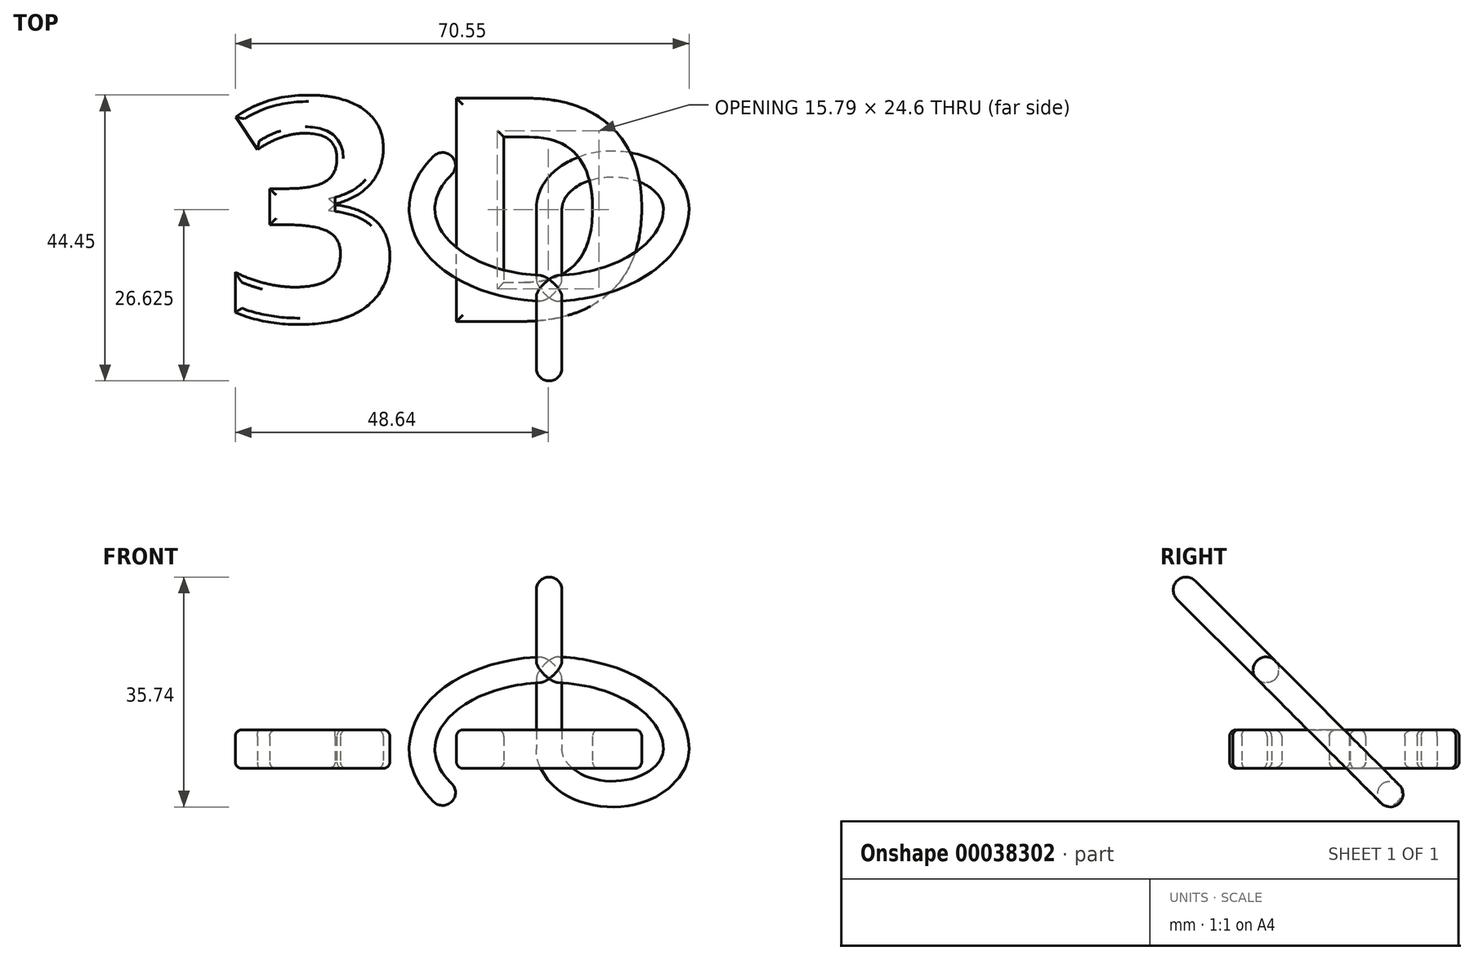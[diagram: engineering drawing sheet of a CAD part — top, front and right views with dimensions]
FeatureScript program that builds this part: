
annotation { "Feature Type Name" : "Feature", "Feature Type Description" : "" }
export const myFeature = defineFeature(function(context is Context, id is Id, definition is map)
    precondition{}
    {
        {
            var Q0;
            Q0=qCreatedBy(makeId("Top.planeOp"),FACE);
            var sketch = newSketch(context, id + "F0", { "sketchPlane" : qUnion([Q0])});
            skText(sketch, "E0", { "text": "3", "fontName": "OpenSans-Bold.ttf"});
            skPoint(sketch, "E1", {"position": v(-17.94, 0) * mm});
            skText(sketch, "E2", { "text": "D", "fontName": "OpenSans-Bold.ttf"});
            skPoint(sketch, "E3", {"position": v(17.58, 0) * mm});
            const initialGuessF0  = {"E0": [-0.03087, -0.0175, 1, 0, 0.035], "E2": [0.001, -0.0175, 1, 0, 0.035]};
            skSetInitialGuess(sketch, initialGuessF0);
            skSolve(sketch);
        }
        {
            var Q0;
            Q0 = qSketchRegion(id + "F0", true);
            extrude(context, id + "F1", {"entities" : qUnion([Q0]), "endBound" : BoundingType.SYMMETRIC, "depth" : 6 * mm});
        }
        {
            var Q0;
            Q0=qCreatedBy(makeId("Front.planeOp"),FACE);
            var sketch = newSketch(context, id + "F2", { "sketchPlane" : qUnion([Q0])});
            skEllipticalArc(sketch, "E4", {});
            skArc(sketch, "E5", {"start": v(19.76, 0) * mm, "mid": v(29.65, -9.88) * mm, "end": v(39.53, 0) * mm});
            skLineSegment(sketch, "E6", {"start": v(19.76, 0) * mm, "end": v(19.76, 35) * mm});
            skPoint(sketch, "E6.endSnap0", {"position": v(19.76, 17.5) * mm});
            skLineSegment(sketch, "E7", {"start": v(19.76, 0) * mm, "end": v(3.2, -9.56) * mm, "construction": true});
            skLineSegment(sketch, "E8", {"start": v(5.37, 0) * mm, "end": v(34.16, 0) * mm, "construction": true});
            const initialGuessF2  = {"E4": [0.0197646484375, 0, 1, 0, 0.0197646484375, 0.0175, 0, 3.71941767693255]};
            skSetInitialGuess(sketch, initialGuessF2);
            skSolve(sketch);
        }
        {
            var Q0;
            Q0=sQuery(id+"F2.wireOp",VERTEX,"E6.end");
            var Q1;
            Q1=qCreatedBy(makeId("Top.planeOp"),FACE);
            cPlane(context, id + "F3", {"entities" : qUnion([Q0, Q1]), "cplaneType" : CPlaneType.PLANE_POINT, "offset" : 150 * mm, "width" : 150 * mm, "height" : 150 * mm});
        }
        {
            var Q0;
            Q0=qCreatedBy(id+"F3.planeOp",FACE);
            var sketch = newSketch(context, id + "F4", { "sketchPlane" : qUnion([Q0])});
            skCircle(sketch, "E9", {"center": v(19.76, 0) * mm, "radius": 2 * mm});
            skSolve(sketch);
        }
        {
            var Q0;
            Q0=makeQuery(id+"F4.imprint","IMPRINT",FACE,{"disambiguationData":[TD([[makeQuery(id+"F4.imprint","IMPRINT",EDGE,{"derivedFrom":sQuery(id+"F4.wireOp",EDGE,"E9")}),1.0]])]});
            var Q1;
            Q1=sQuery(id+"F2.wireOp",EDGE,"E6");
            var Q2;
            Q2=sQuery(id+"F2.wireOp",EDGE,"E5");
            sweep(context, id + "F5", {"profiles" : qUnion([Q0]), "path" : qUnion([Q1, Q2])});
        }
        {
            var Q0;
            Q0=makeQuery(id+"F5.opSweep","CAP_FACE",FACE,{"disambiguationData":[OSD([sQuery(id+"F2.wireOp",VERTEX,"E5.end"),sQuery(id+"F4.wireOp",EDGE,"E9")])],"isStart":false});
            var Q1;
            Q1=sQuery(id+"F2.wireOp",EDGE,"E4");
            sweep(context, id + "F6", {"operationType" : NewBodyOperationType.ADD, "profiles" : qUnion([Q0]), "path" : qUnion([Q1])});
        }
        {
            var Q0;
            Q0=makeQuery(id+"F5.opSweep","CAP_FACE",FACE,{"disambiguationData":[OSD([sQuery(id+"F2.wireOp",VERTEX,"E6.end"),sQuery(id+"F4.wireOp",EDGE,"E9")])],"isStart":true});
            var sketch = newSketch(context, id + "F7", { "sketchPlane" : qUnion([Q0])});
            skLineSegment(sketch, "E10", {"start": v(17.76, 0) * mm, "end": v(21.76, 0) * mm});
            skSolve(sketch);
        }
        {
            var Q0;
            {var subQ1=sQuery(id+"F7.wireOp",EDGE,"E10");Q0=makeQuery(id+"F7.imprint","IMPRINT",FACE,{"disambiguationData":[TD([[makeQuery(id+"F7.imprint","IMPRINT",EDGE,{"derivedFrom":subQ1}),-1.0]])]});}
            var Q1;
            Q1=sQuery(id+"F7.wireOp",EDGE,"E10");
            revolve(context, id + "F8", {"operationType" : NewBodyOperationType.ADD, "entities" : qUnion([Q0]), "axis" : qUnion([Q1]), "revolveType" : RevolveType.FULL});
        }
        {
            var Q0;
            Q0=makeQuery(id+"F6.opSweep","CAP_FACE",FACE,{"disambiguationData":[OSD([sQuery(id+"F2.wireOp",VERTEX,"E4.end"),sQuery(id+"F2.wireOp",VERTEX,"E5.end"),sQuery(id+"F4.wireOp",EDGE,"E9")])],"isStart":false});
            var sketch = newSketch(context, id + "F9", { "sketchPlane" : qUnion([Q0])});
            skLineSegment(sketch, "E11", {"start": v(-3.08, 2) * mm, "end": v(-3.08, -2) * mm});
            skSolve(sketch);
        }
        {
            var Q0;
            {var subQ1=sQuery(id+"F9.wireOp",EDGE,"E11");Q0=makeQuery(id+"F9.imprint","IMPRINT",FACE,{"disambiguationData":[TD([[makeQuery(id+"F9.imprint","IMPRINT",EDGE,{"derivedFrom":subQ1}),-1.0]])]});}
            var Q1;
            Q1=sQuery(id+"F9.wireOp",EDGE,"E11");
            revolve(context, id + "F10", {"operationType" : NewBodyOperationType.ADD, "entities" : qUnion([Q0]), "axis" : qUnion([Q1]), "revolveType" : RevolveType.FULL});
        }
        {
            var Q0;
            Q0=makeQuery(id+"F5.opSweep","SWEPT_BODY",BODY,{"disambiguationData":[OSD([sQuery(id+"F2.wireOp",EDGE,"E5"),sQuery(id+"F4.wireOp",EDGE,"E9")])]});
            var Q1;
            Q1=sQuery(id+"F2.wireOp",EDGE,"E8");
            transform(context, id + "F11", {"entities" : qUnion([Q0]), "transformType" : TransformType.ROTATION, "transformAxis" : qUnion([Q1]), "angle" : 45 * degree, "makeCopy" : false});
        }
        {
            var Q0;
            Q0=makeQuery(id+"F1.opExtrude","CAP_EDGE",EDGE,{"disambiguationData":[OSD([sQuery(id+"F0.wireOp",EDGE,"E0.sketch_text.stroke-6")])],"isStart":false});
            var Q1;
            Q1=makeQuery(id+"F1.opExtrude","CAP_EDGE",EDGE,{"disambiguationData":[OSD([sQuery(id+"F0.wireOp",EDGE,"E0.sketch_text.stroke-0")])],"isStart":false});
            var Q2;
            Q2=makeQuery(id+"F1.opExtrude","CAP_EDGE",EDGE,{"disambiguationData":[OSD([sQuery(id+"F0.wireOp",EDGE,"E0.sketch_text.stroke-23")])],"isStart":false});
            var Q3;
            Q3=makeQuery(id+"F1.opExtrude","CAP_EDGE",EDGE,{"disambiguationData":[OSD([sQuery(id+"F0.wireOp",EDGE,"E0.sketch_text.stroke-21")])],"isStart":false});
            var Q4;
            Q4=makeQuery(id+"F1.opExtrude","CAP_EDGE",EDGE,{"disambiguationData":[OSD([sQuery(id+"F0.wireOp",EDGE,"E0.sketch_text.stroke-16")])],"isStart":false});
            var Q5;
            Q5=makeQuery(id+"F1.opExtrude","CAP_EDGE",EDGE,{"disambiguationData":[OSD([sQuery(id+"F0.wireOp",EDGE,"E0.sketch_text.stroke-14")])],"isStart":false});
            var Q6;
            Q6=makeQuery(id+"F1.opExtrude","CAP_EDGE",EDGE,{"disambiguationData":[OSD([sQuery(id+"F0.wireOp",EDGE,"E0.sketch_text.stroke-8")])],"isStart":false});
            var Q7;
            Q7=makeQuery(id+"F1.opExtrude","CAP_EDGE",EDGE,{"disambiguationData":[OSD([sQuery(id+"F0.wireOp",EDGE,"E0.sketch_text.stroke-30")])],"isStart":false});
            var Q8;
            Q8=makeQuery(id+"F1.opExtrude","CAP_EDGE",EDGE,{"disambiguationData":[OSD([sQuery(id+"F0.wireOp",EDGE,"E0.sketch_text.stroke-31")])],"isStart":false});
            var Q9;
            Q9=makeQuery(id+"F1.opExtrude","CAP_EDGE",EDGE,{"disambiguationData":[OSD([sQuery(id+"F0.wireOp",EDGE,"E0.sketch_text.stroke-36")])],"isStart":false});
            var Q10;
            Q10=makeQuery(id+"F1.opExtrude","CAP_EDGE",EDGE,{"disambiguationData":[OSD([sQuery(id+"F0.wireOp",EDGE,"E0.sketch_text.stroke-35")])],"isStart":false});
            var Q11;
            Q11=makeQuery(id+"F1.opExtrude","CAP_FACE",FACE,{"disambiguationData":[OSD([sQuery(id+"F0.wireOp",EDGE,"E0.sketch_text.stroke-27"),sQuery(id+"F0.wireOp",EDGE,"E0.sketch_text.stroke-28"),sQuery(id+"F0.wireOp",EDGE,"E0.sketch_text.stroke-29"),sQuery(id+"F0.wireOp",EDGE,"E0.sketch_text.stroke-30"),sQuery(id+"F0.wireOp",EDGE,"E0.sketch_text.stroke-31"),sQuery(id+"F0.wireOp",EDGE,"E0.sketch_text.stroke-32"),sQuery(id+"F0.wireOp",EDGE,"E0.sketch_text.stroke-33"),sQuery(id+"F0.wireOp",EDGE,"E0.sketch_text.stroke-34"),sQuery(id+"F0.wireOp",EDGE,"E0.sketch_text.stroke-35"),sQuery(id+"F0.wireOp",EDGE,"E0.sketch_text.stroke-36"),sQuery(id+"F0.wireOp",EDGE,"E0.sketch_text.stroke-37"),sQuery(id+"F0.wireOp",EDGE,"E0.sketch_text.stroke-38")])],"isStart":true});
            var Q12;
            Q12=makeQuery(id+"F1.opExtrude","CAP_FACE",FACE,{"disambiguationData":[OSD([sQuery(id+"F0.wireOp",EDGE,"E0.sketch_text.stroke-0"),sQuery(id+"F0.wireOp",EDGE,"E0.sketch_text.stroke-1"),sQuery(id+"F0.wireOp",EDGE,"E0.sketch_text.stroke-2"),sQuery(id+"F0.wireOp",EDGE,"E0.sketch_text.stroke-3"),sQuery(id+"F0.wireOp",EDGE,"E0.sketch_text.stroke-4"),sQuery(id+"F0.wireOp",EDGE,"E0.sketch_text.stroke-5"),sQuery(id+"F0.wireOp",EDGE,"E0.sketch_text.stroke-6"),sQuery(id+"F0.wireOp",EDGE,"E0.sketch_text.stroke-7"),sQuery(id+"F0.wireOp",EDGE,"E0.sketch_text.stroke-8"),sQuery(id+"F0.wireOp",EDGE,"E0.sketch_text.stroke-9"),sQuery(id+"F0.wireOp",EDGE,"E0.sketch_text.stroke-10"),sQuery(id+"F0.wireOp",EDGE,"E0.sketch_text.stroke-11"),sQuery(id+"F0.wireOp",EDGE,"E0.sketch_text.stroke-12"),sQuery(id+"F0.wireOp",EDGE,"E0.sketch_text.stroke-13"),sQuery(id+"F0.wireOp",EDGE,"E0.sketch_text.stroke-14"),sQuery(id+"F0.wireOp",EDGE,"E0.sketch_text.stroke-15"),sQuery(id+"F0.wireOp",EDGE,"E0.sketch_text.stroke-16"),sQuery(id+"F0.wireOp",EDGE,"E0.sketch_text.stroke-17"),sQuery(id+"F0.wireOp",EDGE,"E0.sketch_text.stroke-18"),sQuery(id+"F0.wireOp",EDGE,"E0.sketch_text.stroke-19"),sQuery(id+"F0.wireOp",EDGE,"E0.sketch_text.stroke-20"),sQuery(id+"F0.wireOp",EDGE,"E0.sketch_text.stroke-21"),sQuery(id+"F0.wireOp",EDGE,"E0.sketch_text.stroke-22"),sQuery(id+"F0.wireOp",EDGE,"E0.sketch_text.stroke-23"),sQuery(id+"F0.wireOp",EDGE,"E0.sketch_text.stroke-24"),sQuery(id+"F0.wireOp",EDGE,"E0.sketch_text.stroke-25"),sQuery(id+"F0.wireOp",EDGE,"E0.sketch_text.stroke-26")])],"isStart":true});
            var Q13;
            Q13=makeQuery(id+"F1.opExtrude","CAP_FACE",FACE,{"disambiguationData":[OSD([sQuery(id+"F0.wireOp",EDGE,"E2.sketch_text.stroke-0"),sQuery(id+"F0.wireOp",EDGE,"E2.sketch_text.stroke-1"),sQuery(id+"F0.wireOp",EDGE,"E2.sketch_text.stroke-2"),sQuery(id+"F0.wireOp",EDGE,"E2.sketch_text.stroke-3"),sQuery(id+"F0.wireOp",EDGE,"E2.sketch_text.stroke-4"),sQuery(id+"F0.wireOp",EDGE,"E2.sketch_text.stroke-5"),sQuery(id+"F0.wireOp",EDGE,"E2.sketch_text.stroke-6"),sQuery(id+"F0.wireOp",EDGE,"E2.sketch_text.stroke-7"),sQuery(id+"F0.wireOp",EDGE,"E2.sketch_text.stroke-8"),sQuery(id+"F0.wireOp",EDGE,"E2.sketch_text.stroke-9"),sQuery(id+"F0.wireOp",EDGE,"E2.sketch_text.stroke-10"),sQuery(id+"F0.wireOp",EDGE,"E2.sketch_text.stroke-11")])],"isStart":false});
            var Q14;
            Q14=makeQuery(id+"F1.opExtrude","CAP_FACE",FACE,{"disambiguationData":[OSD([sQuery(id+"F0.wireOp",EDGE,"E2.sketch_text.stroke-0"),sQuery(id+"F0.wireOp",EDGE,"E2.sketch_text.stroke-1"),sQuery(id+"F0.wireOp",EDGE,"E2.sketch_text.stroke-2"),sQuery(id+"F0.wireOp",EDGE,"E2.sketch_text.stroke-3"),sQuery(id+"F0.wireOp",EDGE,"E2.sketch_text.stroke-4"),sQuery(id+"F0.wireOp",EDGE,"E2.sketch_text.stroke-5"),sQuery(id+"F0.wireOp",EDGE,"E2.sketch_text.stroke-6"),sQuery(id+"F0.wireOp",EDGE,"E2.sketch_text.stroke-7"),sQuery(id+"F0.wireOp",EDGE,"E2.sketch_text.stroke-8"),sQuery(id+"F0.wireOp",EDGE,"E2.sketch_text.stroke-9"),sQuery(id+"F0.wireOp",EDGE,"E2.sketch_text.stroke-10"),sQuery(id+"F0.wireOp",EDGE,"E2.sketch_text.stroke-11")])],"isStart":true});
            fillet(context, id + "F12", {"entities" : qUnion([Q0, Q1, Q2, Q3, Q4, Q5, Q6, Q7, Q8, Q9, Q10, Q11, Q12, Q13, Q14]), "radius" : 1 * mm, "tangentPropagation" : true, "allowEdgeOverflow" : false});
        }
    });
